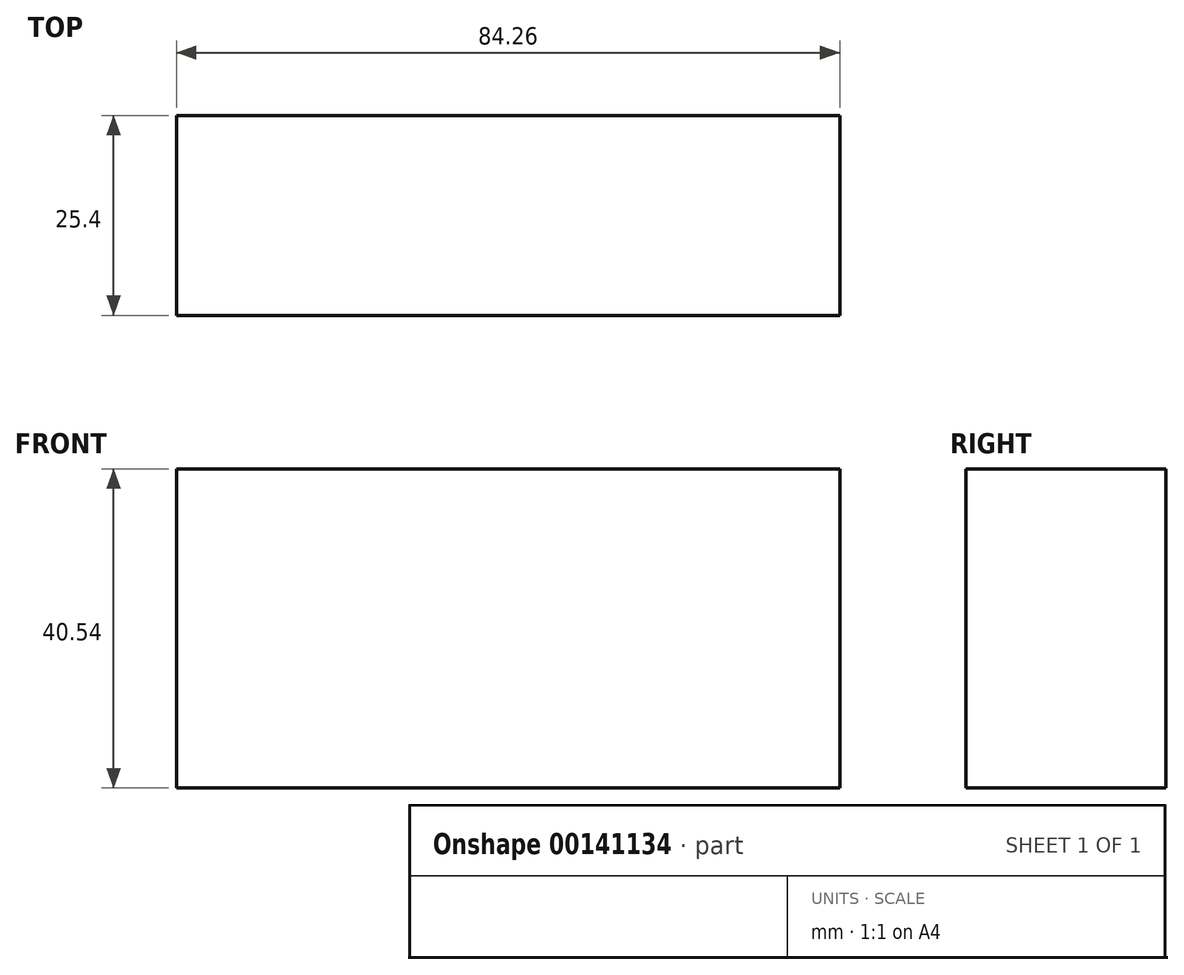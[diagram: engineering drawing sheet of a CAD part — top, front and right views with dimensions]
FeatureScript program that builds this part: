
annotation { "Feature Type Name" : "Feature", "Feature Type Description" : "" }
export const myFeature = defineFeature(function(context is Context, id is Id, definition is map)
    precondition{}
    {
        {
            var Q0;
            Q0=qCreatedBy(makeId("Front.planeOp"),FACE);
            var sketch = newSketch(context, id + "F0", { "sketchPlane" : qUnion([Q0])});
            skLineSegment(sketch, "E0.bottom", {"start": v(0, 0) * mm, "end": v(84.26, 0) * mm});
            skLineSegment(sketch, "E0.top", {"start": v(0, 40.54) * mm, "end": v(84.26, 40.54) * mm});
            skLineSegment(sketch, "E0.left", {"start": v(0, 0) * mm, "end": v(0, 40.54) * mm});
            skLineSegment(sketch, "E0.right", {"start": v(84.26, 0) * mm, "end": v(84.26, 40.54) * mm});
            skSolve(sketch);
        }
        {
            var Q0;
            Q0 = qSketchRegion(id + "F0", true);
            extrude(context, id + "F1", {"entities" : qUnion([Q0]), "depth" : 25.4 * mm});
        }
    });
